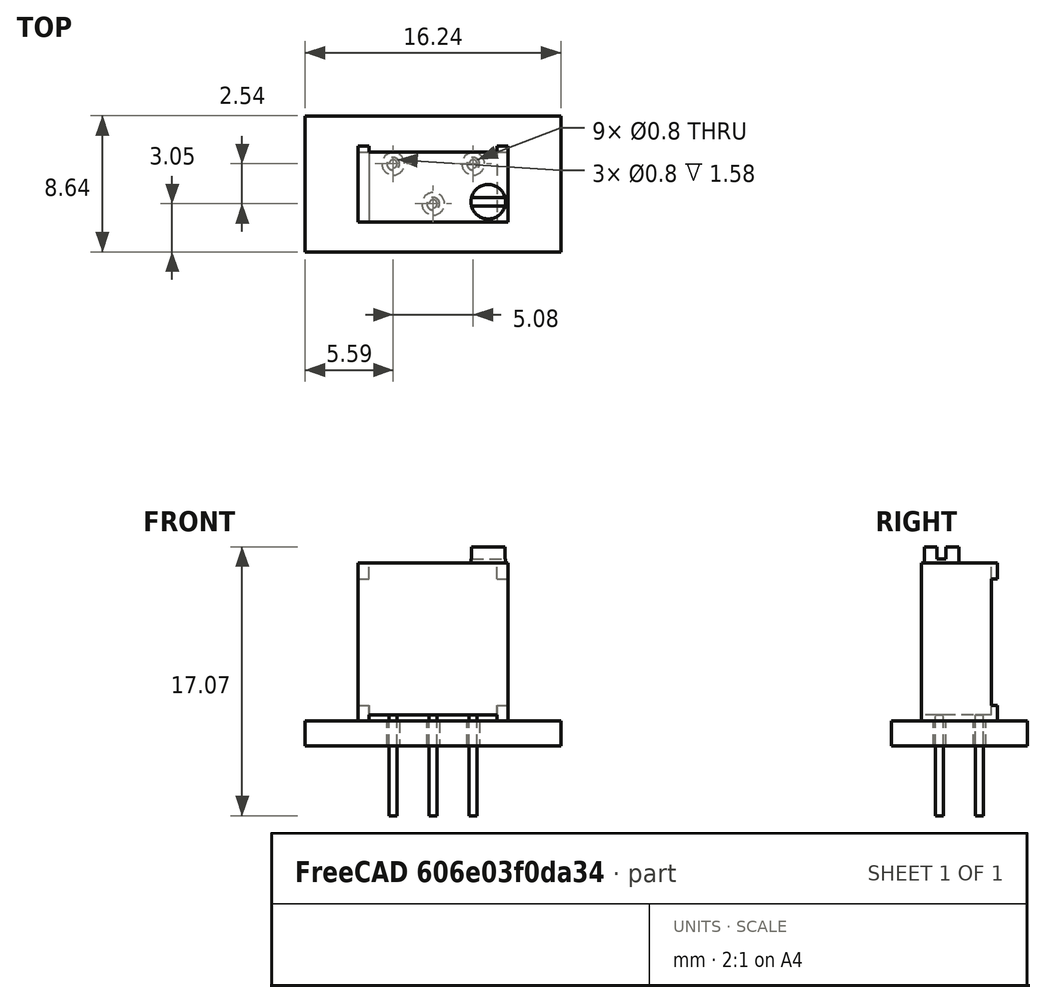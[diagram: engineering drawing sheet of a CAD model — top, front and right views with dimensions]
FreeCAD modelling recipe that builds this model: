
FCSTD DOCUMENT  (FreeCAD 0.18R15611 (Git))
Label: Potentiometer_Bourns_3296Y_Vertical
License: All rights reserved
LicenseURL: http://en.wikipedia.org/wiki/All_rights_reserved
objects: Part::FeaturePython×7, Part::Box×6, Part::Cylinder×4, Part::MultiFuse×2, App::DocumentObjectGroup×1, Part::Cut×1, Part::Feature×1
note: 21 computed .brp shape members not serialized (recipe doc carries the construction recipe); baked Part::Feature solids carry a one-line shape summary decoded from their .brp

FEATURE [Part::FeaturePython] FCrtYd_lines  label="FCrtYd"  # a2plus imported part (geometry in sourceFile) (typed FeaturePython)
  fixedPosition = true
FEATURE [Part::FeaturePython] FFab_lines  label="FFab"  # a2plus imported part (geometry in sourceFile) (typed FeaturePython)
  fixedPosition = true
FEATURE [Part::FeaturePython] Filk_lines  label="FrontSilk"  # a2plus imported part (geometry in sourceFile) (typed FeaturePython)
  fixedPosition = true
FEATURE [Part::FeaturePython] TopPads  # a2plus imported part (geometry in sourceFile) (typed FeaturePython)
  fixedPosition = true
FEATURE [Part::FeaturePython] BotPads  # a2plus imported part (geometry in sourceFile) (typed FeaturePython)
  fixedPosition = true
FEATURE [Part::FeaturePython] THPs  label="PTHs"  # a2plus imported part (geometry in sourceFile) (typed FeaturePython)
  fixedPosition = true
FEATURE [Part::FeaturePython] newPCB  label="Pcb"  # a2plus imported part (geometry in sourceFile) (typed FeaturePython)
  fixedPosition = true
FEATURE [App::DocumentObjectGroup] Potentiometer_Bourns_3296Y_Vertical_fp
  Group = -> [FCrtYd_lines,FFab_lines,Filk_lines,TopPads,BotPads,THPs,newPCB]
FEATURE [Part::Box] Box004  label="StandoffFront"
  AttacherType = Attacher::AttachEngine3D
  Height = 4.83
  Length = 1
  Width = 0.7
FEATURE [Part::Box] Box005  label="StandoffBack"
  AttacherType = Attacher::AttachEngine3D
  Height = 4.83
  Length = 1
  Placement = pos=(9.03,0,0) rot=(0,0,1;0rad)
  Width = 0.7
FEATURE [Part::Cylinder] Cylinder001  label="Pin3"
  Angle = 360
  AttacherType = Attacher::AttachEngine3D
  Height = 6.4
  Placement = pos=(-5.08,0,-6.02) rot=(0,0,1;0rad)
  Radius = 0.255
FEATURE [Part::Box] Box006  label="StandoffFront001"
  AttacherType = Attacher::AttachEngine3D
  Height = 4.83
  Length = 1
  Placement = pos=(0,8.83,0) rot=(0,0,1;0rad)
  Width = 0.7
FEATURE [Part::Box] Box007  label="StandoffBack001"
  AttacherType = Attacher::AttachEngine3D
  Height = 4.83
  Length = 1
  Placement = pos=(9.03,8.83,0) rot=(0,0,1;0rad)
  Width = 0.7
FEATURE [Part::Box] Box  label="Body"
  AttacherType = Attacher::AttachEngine3D
  Height = 4.45
  Length = 9.65
  Placement = pos=(0,0,0.38) rot=(0,0,1;0rad)
  Width = 9.53
FEATURE [Part::MultiFuse] Fusion  label="FusionBody"
  Placement = pos=(-7.305,1.14,10.03) rot=(0.57735,0.57735,-0.57735;2.0944rad)
  Refine = true
  Shapes = -> [Box,Box004,Box005,Box006,Box007]
FEATURE [Part::Cylinder] Cylinder  label="Pin1"
  Angle = 360
  AttacherType = Attacher::AttachEngine3D
  Height = 6.4
  Placement = pos=(0,0,-6.02) rot=(0,0,1;0rad)
  Radius = 0.255
FEATURE [Part::Cylinder] Cylinder002  label="Pin2"
  Angle = 360
  AttacherType = Attacher::AttachEngine3D
  Height = 6.4
  Placement = pos=(-2.54,-2.54,-6.02) rot=(0,0,1;0rad)
  Radius = 0.255
FEATURE [Part::Cylinder] Cylinder003  label="Knob"
  Angle = 360
  AttacherType = Attacher::AttachEngine3D
  Height = 1.02
  Placement = pos=(-0.405,-2.25,7.24) rot=(0,0,1;0rad)
  Radius = 1.095
FEATURE [Part::Box] Box003  label="Cube001"
  AttacherType = Attacher::AttachEngine3D
  Height = 0.76
  Length = 10
  Placement = pos=(-5,-2.54,7.5) rot=(0,0,1;0rad)
  Width = 0.56
FEATURE [Part::Cut] Cut  label="CutKnob"
  Base = -> Cylinder003
  Placement = pos=(1.36,-0.16,2.79) rot=(0,-1,0;0rad)
  Refine = true
  Tool = -> Box003
FEATURE [Part::MultiFuse] Pin2_mp_cp  label="Pin2_fd"
  Refine = true
  Shapes = -> [Cylinder002,Cylinder,Cylinder001,Cut,Fusion]
FEATURE [Part::Feature] Shape  label="Potentiometer_Bourns_3296Y_Vertical"
  shape: bbox 9.53 x 4.83 x 17.07 mm, 32 faces (baked)
